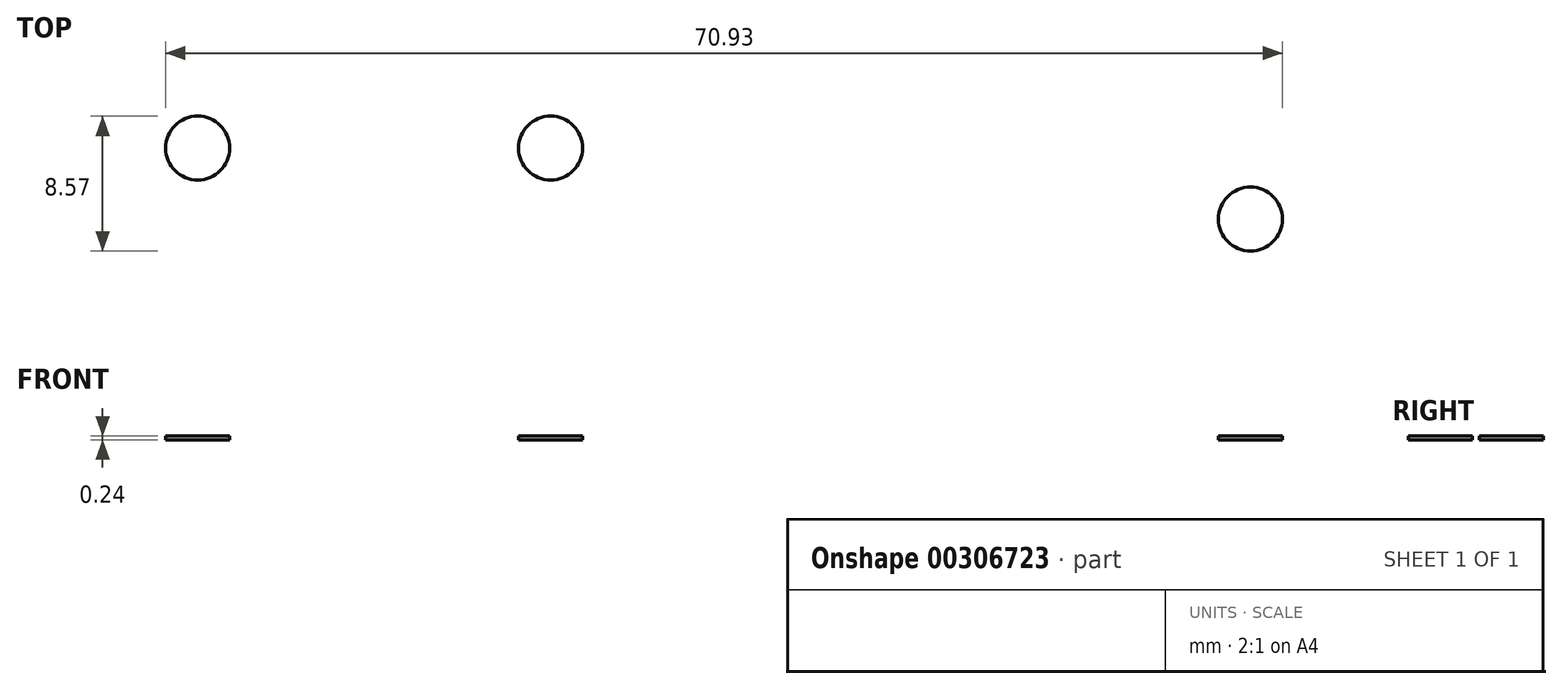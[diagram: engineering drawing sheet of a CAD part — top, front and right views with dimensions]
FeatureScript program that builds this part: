
annotation { "Feature Type Name" : "Feature", "Feature Type Description" : "" }
export const myFeature = defineFeature(function(context is Context, id is Id, definition is map)
    precondition{}
    {
        {
            var Q0;
            Q0=qCreatedBy(makeId("Top.planeOp"),FACE);
            var sketch = newSketch(context, id + "F0", { "sketchPlane" : qUnion([Q0])});
            skLineSegment(sketch, "E0.bottom", {"start": v(63.5, 38.1) * mm, "end": v(-63.5, 38.1) * mm});
            skLineSegment(sketch, "E0.top", {"start": v(63.5, -38.1) * mm, "end": v(-63.5, -38.1) * mm});
            skLineSegment(sketch, "E0.left", {"start": v(63.5, 38.1) * mm, "end": v(63.5, -38.1) * mm});
            skLineSegment(sketch, "E0.right", {"start": v(-63.5, 38.1) * mm, "end": v(-63.5, -38.1) * mm});
            skPoint(sketch, "E0.middle", {"position": v(0, 0) * mm});
            skSolve(sketch);
        }
        {
            assignVariable(context, id + "F1", {"name" : "mdfThick", "anyValue" : .235});
        }
        {
            var Q0;
            Q0 = qSketchRegion(id + "F0", true);
            extrude(context, id + "F2", {"entities" : qUnion([Q0]), "depth" : (getVariable(context, 'mdfThick')) * mm});
        }
        {
            var Q0;
            Q0=makeQuery(id+"F2.opExtrude","CAP_FACE",FACE,{"disambiguationData":[OSD([sQuery(id+"F0.wireOp",EDGE,"E0.bottom"),sQuery(id+"F0.wireOp",EDGE,"E0.top"),sQuery(id+"F0.wireOp",EDGE,"E0.left"),sQuery(id+"F0.wireOp",EDGE,"E0.right")])],"isStart":false});
            var sketch = newSketch(context, id + "F3", { "sketchPlane" : qUnion([Q0])});
            skLineSegment(sketch, "E1", {"start": v(0, 0) * mm, "end": v(-19.05, 0) * mm});
            skLineSegment(sketch, "E2", {"start": v(-19.05, 0) * mm, "end": v(-19.05, -29.9) * mm});
            skCircle(sketch, "E3", {"center": v(-19.05, -29.9) * mm, "radius": 2.03 * mm});
            skLineSegment(sketch, "E4", {"start": v(-19.05, 0) * mm, "end": v(-41.47, 0) * mm});
            skPoint(sketch, "E4.endSnap0", {"position": v(-63.5, 0) * mm});
            skLineSegment(sketch, "E5", {"start": v(-41.47, 0) * mm, "end": v(-41.47, -29.9) * mm});
            skCircle(sketch, "E6", {"center": v(-41.47, -29.9) * mm, "radius": 2.03 * mm});
            skLineSegment(sketch, "E7", {"start": v(0, 0) * mm, "end": v(25.4, 0) * mm});
            skLineSegment(sketch, "E8", {"start": v(25.4, 0) * mm, "end": v(25.4, -25.4) * mm});
            skLineSegment(sketch, "E9", {"start": v(25.4, 0) * mm, "end": v(6.35, 0) * mm});
            skCircle(sketch, "E10", {"center": v(6.35, 0) * mm, "radius": 2.03 * mm});
            skCircle(sketch, "E11", {"center": v(25.4, -25.4) * mm, "radius": 2.03 * mm});
            skLineSegment(sketch, "E12", {"start": v(25.4, 0) * mm, "end": v(19.05, 0) * mm});
            skCircle(sketch, "E13.MirrorC", {"center": v(-41.47, 29.9) * mm, "radius": 2.03 * mm});
            skCircle(sketch, "E14.MirrorC", {"center": v(-19.05, 29.9) * mm, "radius": 2.03 * mm});
            skCircle(sketch, "E15.MirrorC", {"center": v(25.4, 25.4) * mm, "radius": 2.03 * mm});
            skSolve(sketch);
        }
        {
            var Q0;
            Q0=makeQuery(id+"F3.imprint","IMPRINT",FACE,{"disambiguationData":[TD([[makeQuery(id+"F3.imprint","IMPRINT",EDGE,{"derivedFrom":sQuery(id+"F3.wireOp",EDGE,"E6")}),1.0]])]});
            var Q1;
            Q1=makeQuery(id+"F3.imprint","IMPRINT",FACE,{"disambiguationData":[TD([[makeQuery(id+"F3.imprint","IMPRINT",EDGE,{"derivedFrom":sQuery(id+"F3.wireOp",EDGE,"E3")}),1.0]])]});
            var Q2;
            {var subQ0=sQuery(id+"F3.wireOp",EDGE,"E9");var subQ1=sQuery(id+"F3.wireOp",EDGE,"E7");var subQ2=makeQuery(id+"F3.imprint","INTERSECT",VERTEX,{"derivedFrom":[subQ1,subQ0]});Q2=makeQuery(id+"F3.imprint","IMPRINT",FACE,{"disambiguationData":[TD([[makeQuery(id+"F3.imprint","IMPRINT",EDGE,{"disambiguationData":[TD([[subQ2,1.0]])],"derivedFrom":subQ1}),-1.0]])]});}
            var Q3;
            {var subQ0=sQuery(id+"F3.wireOp",EDGE,"E9");var subQ1=sQuery(id+"F3.wireOp",EDGE,"E7");var subQ2=makeQuery(id+"F3.imprint","INTERSECT",VERTEX,{"derivedFrom":[subQ1,subQ0]});Q3=makeQuery(id+"F3.imprint","IMPRINT",FACE,{"disambiguationData":[TD([[makeQuery(id+"F3.imprint","IMPRINT",EDGE,{"disambiguationData":[TD([[subQ2,1.0]])],"derivedFrom":subQ1}),1.0]])]});}
            var Q4;
            Q4=makeQuery(id+"F3.imprint","IMPRINT",FACE,{"disambiguationData":[TD([[makeQuery(id+"F3.imprint","IMPRINT",EDGE,{"derivedFrom":sQuery(id+"F3.wireOp",EDGE,"E11")}),1.0]])]});
            var Q5;
            Q5=makeQuery(id+"F3.imprint","IMPRINT",FACE,{"disambiguationData":[TD([[makeQuery(id+"F3.imprint","IMPRINT",EDGE,{"derivedFrom":sQuery(id+"F3.wireOp",EDGE,"E13.MirrorC")}),-1.0]])]});
            var Q6;
            Q6=makeQuery(id+"F3.imprint","IMPRINT",FACE,{"disambiguationData":[TD([[makeQuery(id+"F3.imprint","IMPRINT",EDGE,{"derivedFrom":sQuery(id+"F3.wireOp",EDGE,"E14.MirrorC")}),-1.0]])]});
            var Q7;
            Q7=makeQuery(id+"F3.imprint","IMPRINT",FACE,{"disambiguationData":[TD([[makeQuery(id+"F3.imprint","IMPRINT",EDGE,{"derivedFrom":sQuery(id+"F3.wireOp",EDGE,"E15.MirrorC")}),-1.0]])]});
            extrude(context, id + "F4", {"entities" : qUnion([Q0, Q1, Q2, Q3, Q4, Q5, Q6, Q7]), "operationType" : NewBodyOperationType.REMOVE, "endBound" : BoundingType.UP_TO_NEXT, "oppositeDirection" : true, "depth" : 25.4 * mm});
        }
    });
